# Revit family: ASL7S
name_source: partatom
category: Lighting Fixtures
revit_build: Autodesk Revit 2014 (Build: 20130308_1515(x64)
units: mm (PartAtom-declared; Revit-internal decimal feet)

## types (1)
- Flush
    Apparent Load = 0 VA
    Assembly Code = D5020200
    Color Filter = 16777215
    Default Elevation = 48 "
    Description = he Steplights collection brings you a full palette of designs with exceptional lighting performance. Choose from 2 shapes, 2 materials, 2 sizes, 3 fascia designs, and 3 mounting options to best suit your applications. AAL's small Steplights are now available with a 5-watt energy-efficient and long life LED system
    Dimming Lamp Color Temperature Shift = <None>
    Emit Shape Visible in Rendering = No
    Emit from Circle Diameter = 8 "
    Glass = Glass - Hubbell - White
    Housing Material = Metal - Hubbell - Aluminum, Anodized Blue
    Lamp = LED
    Length = 0 "
    Load Classification = Lighting
    Manufacturer = Architectural Arealighting
    Model = Steplights 7 Small
    Mounting = Wall
    Photometric Link = https://www.hubbell.com
    Photometric Notes = More IES files download on Photometric Link
    Photometric Web File = ASL7-RD-EYE-LV50.IES
    Power Factor = 1
    Product Documentation Link = https://hubbellcdn.com
    Product Page URL = https://www.hubbell.com
    Tilt Angle = -180.00°
    Type Comments = Lighting Fixture
    URL = https://www.hubbell.com
    Voltage = 120 V
    Warranty = 5-Years Warranty
    Wattage Comments = 12W
    second end = 0.01 "

## geometry (parser evidence)
native form markers: Sweep x4
no freeform markers — native parametric forms only
